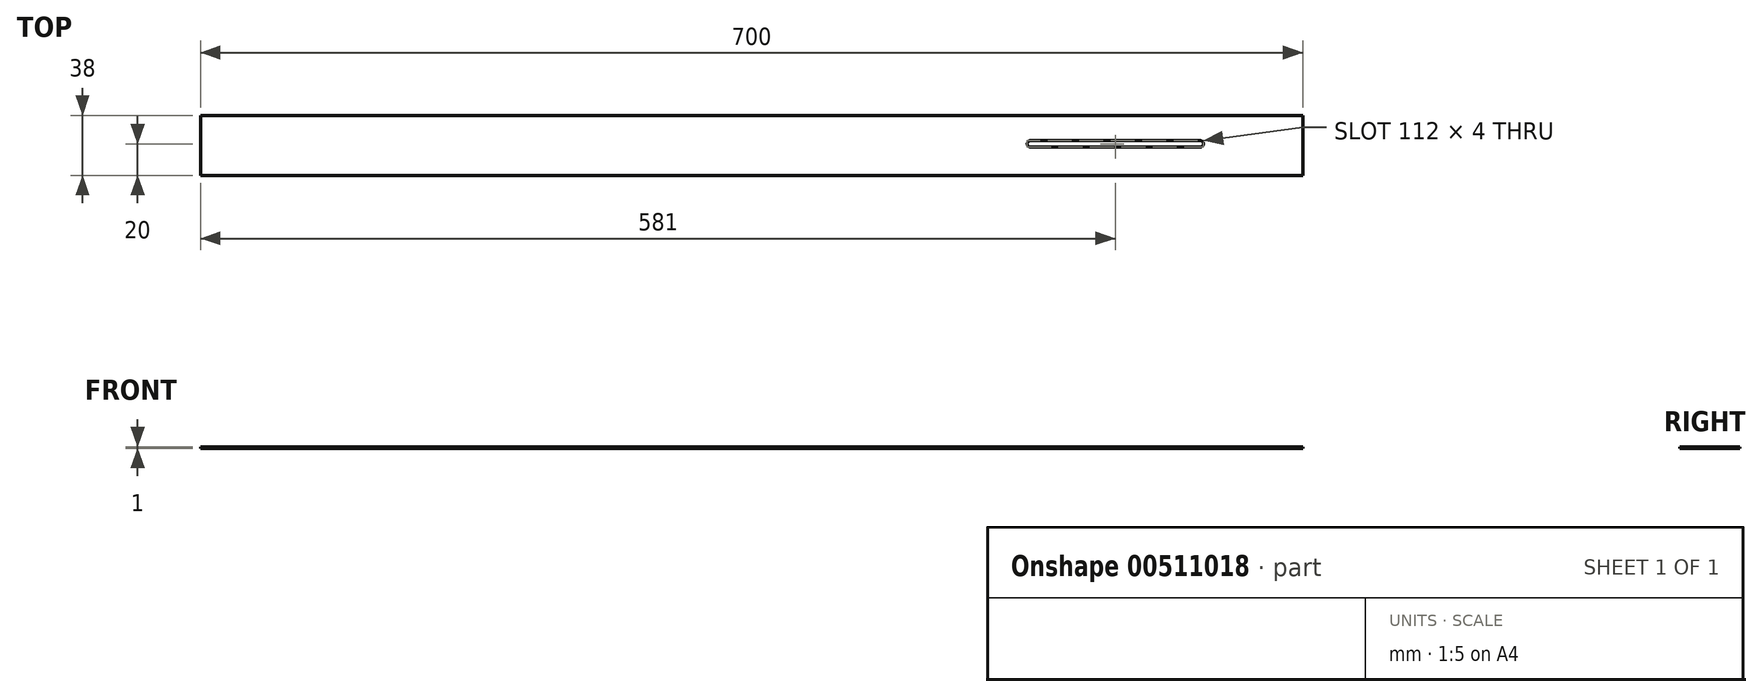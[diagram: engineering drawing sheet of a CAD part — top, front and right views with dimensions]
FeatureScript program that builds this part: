
annotation { "Feature Type Name" : "Feature", "Feature Type Description" : "" }
export const myFeature = defineFeature(function(context is Context, id is Id, definition is map)
    precondition{}
    {
        {
            var Q0;
            Q0=qCreatedBy(makeId("Top.planeOp"),FACE);
            var sketch = newSketch(context, id + "F0", { "sketchPlane" : qUnion([Q0])});
            skLineSegment(sketch, "E0.bottom", {"start": v(-350, 19) * mm, "end": v(350, 19) * mm});
            skLineSegment(sketch, "E0.top", {"start": v(-350, -19) * mm, "end": v(350, -19) * mm});
            skLineSegment(sketch, "E0.left", {"start": v(-350, 19) * mm, "end": v(-350, -19) * mm});
            skLineSegment(sketch, "E0.right", {"start": v(350, 19) * mm, "end": v(350, -19) * mm});
            skSolve(sketch);
        }
        {
            var Q0;
            Q0=makeQuery(id+"F0.imprint","IMPRINT",FACE,{"disambiguationData":[TD([[makeQuery(id+"F0.imprint","IMPRINT",EDGE,{"derivedFrom":sQuery(id+"F0.wireOp",EDGE,"E0.bottom")}),-1.0]])]});
            extrude(context, id + "F1", {"entities" : qUnion([Q0]), "depth" : 1 * mm});
        }
        {
            var Q0;
            Q0=makeQuery(id+"F1.opExtrude","CAP_FACE",FACE,{"disambiguationData":[OSD([sQuery(id+"F0.wireOp",EDGE,"E0.bottom"),sQuery(id+"F0.wireOp",EDGE,"E0.top"),sQuery(id+"F0.wireOp",EDGE,"E0.left"),sQuery(id+"F0.wireOp",EDGE,"E0.right")])],"isStart":false});
            var sketch = newSketch(context, id + "F2", { "sketchPlane" : qUnion([Q0])});
            skLineSegment(sketch, "E1.bottom", {"start": v(177, 3) * mm, "end": v(285, 3) * mm});
            skLineSegment(sketch, "E1.top", {"start": v(177, -1) * mm, "end": v(285, -1) * mm});
            skLineSegment(sketch, "E1.left", {"start": v(175, 1) * mm, "end": v(175, 1) * mm});
            skLineSegment(sketch, "E1.right", {"start": v(287, 1) * mm, "end": v(287, 1) * mm});
            skPoint(sketch, "E2.visualSharp", {"position": v(175, 3) * mm});
            skArc(sketch, "E2.filletArc", {"start": v(177, 3) * mm, "mid": v(175.59, 2.41) * mm, "end": v(175, 1) * mm});
            skPoint(sketch, "E3.visualSharp", {"position": v(175, -1) * mm});
            skArc(sketch, "E3.filletArc", {"start": v(175, 1) * mm, "mid": v(175.59, -0.41) * mm, "end": v(177, -1) * mm});
            skPoint(sketch, "E4.visualSharp", {"position": v(287, 3) * mm});
            skArc(sketch, "E4.filletArc", {"start": v(287, 1) * mm, "mid": v(286.41, 2.41) * mm, "end": v(285, 3) * mm});
            skPoint(sketch, "E5.visualSharp", {"position": v(287, -1) * mm});
            skArc(sketch, "E5.filletArc", {"start": v(285, -1) * mm, "mid": v(286.41, -0.41) * mm, "end": v(287, 1) * mm});
            skSolve(sketch);
        }
        {
            var Q0;
            Q0=makeQuery(id+"F2.imprint","IMPRINT",FACE,{"disambiguationData":[TD([[makeQuery(id+"F2.imprint","IMPRINT",EDGE,{"derivedFrom":sQuery(id+"F2.wireOp",EDGE,"E1.bottom")}),-1.0]])]});
            extrude(context, id + "F3", {"entities" : qUnion([Q0]), "operationType" : NewBodyOperationType.REMOVE, "oppositeDirection" : true, "depth" : 1 * mm});
        }
    });
